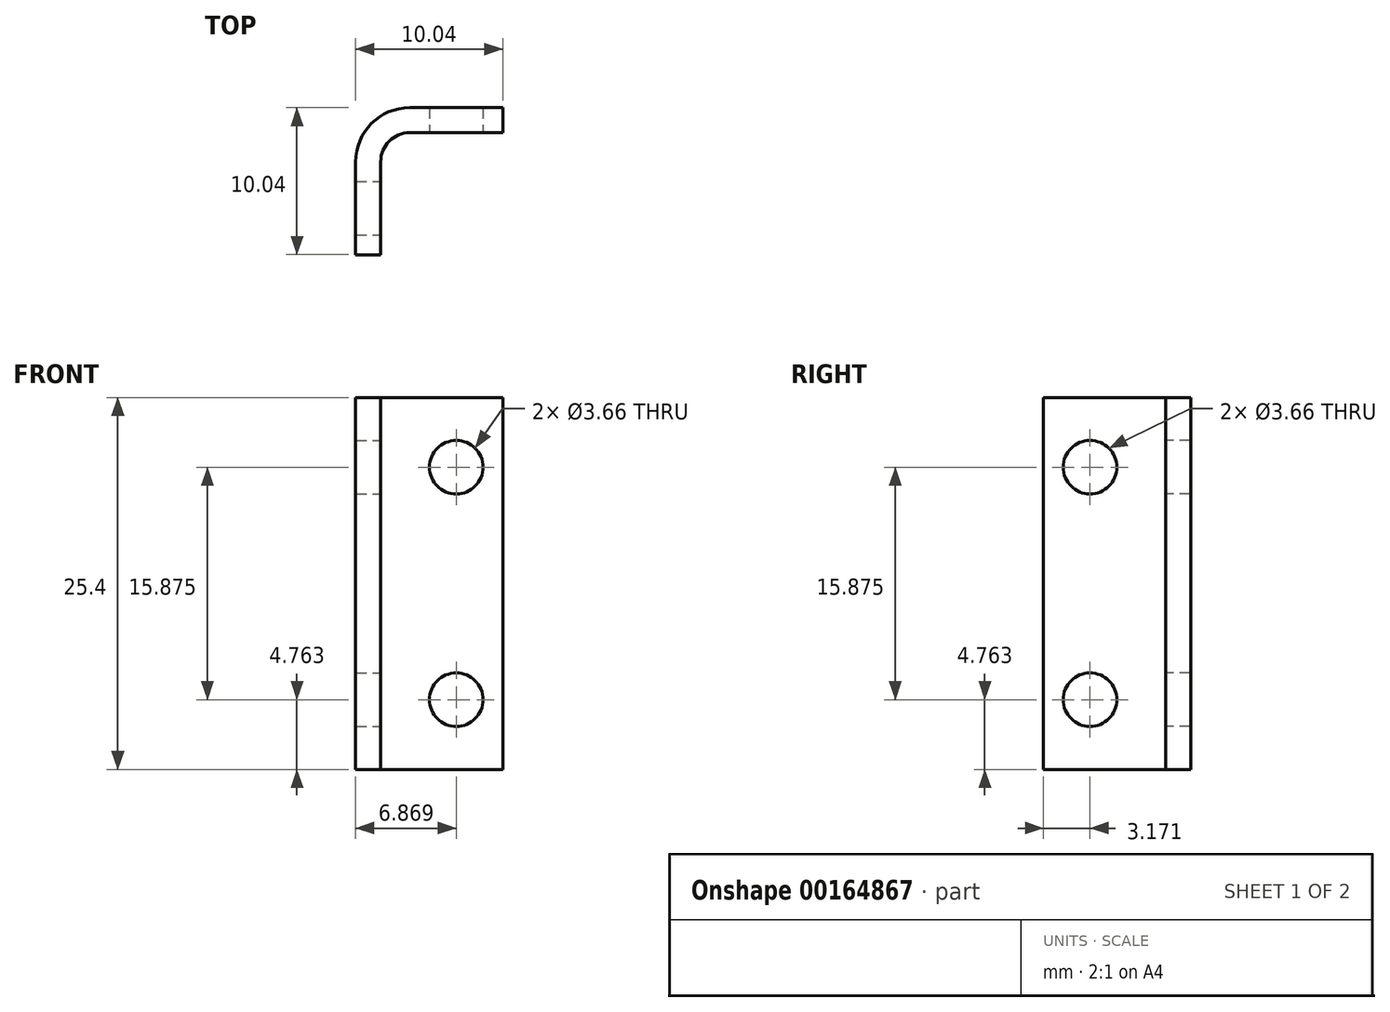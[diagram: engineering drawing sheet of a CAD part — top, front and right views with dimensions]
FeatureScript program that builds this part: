
annotation { "Feature Type Name" : "Feature", "Feature Type Description" : "" }
export const myFeature = defineFeature(function(context is Context, id is Id, definition is map)
    precondition{}
    {
        {
            var Q0;
            Q0=qCreatedBy(makeId("Top.planeOp"),FACE);
            var sketch = newSketch(context, id + "F0", { "sketchPlane" : qUnion([Q0])});
            skLineSegment(sketch, "E0.top", {"start": v(0, -8.33) * mm, "end": v(-1.7, -8.33) * mm});
            skLineSegment(sketch, "E0.left", {"start": v(0, 0) * mm, "end": v(0, -8.33) * mm});
            skLineSegment(sketch, "E0.right", {"start": v(-1.7, 1.7) * mm, "end": v(-1.7, -8.33) * mm});
            skLineSegment(sketch, "E1.bottom", {"start": v(0, 0) * mm, "end": v(8.33, 0) * mm});
            skLineSegment(sketch, "E1.top", {"start": v(-1.7, 1.7) * mm, "end": v(8.33, 1.7) * mm});
            skLineSegment(sketch, "E1.right", {"start": v(8.33, 0) * mm, "end": v(8.33, 1.7) * mm});
            skSolve(sketch);
        }
        {
            var Q0;
            Q0 = qSketchRegion(id + "F0", true);
            extrude(context, id + "F1", {"entities" : qUnion([Q0]), "depth" : 25.4 * mm});
        }
        {
            var Q0;
            Q0=makeQuery(id+"F1.opExtrude","SWEPT_FACE",FACE,{"disambiguationData":[OSD([sQuery(id+"F0.wireOp",EDGE,"E1.bottom")])]});
            var sketch = newSketch(context, id + "F2", { "sketchPlane" : qUnion([Q0])});
            skLineSegment(sketch, "E2.bottom", {"start": v(8.33, 25.4) * mm, "end": v(5.16, 25.4) * mm, "construction": true});
            skLineSegment(sketch, "E2.top", {"start": v(8.33, 20.64) * mm, "end": v(5.16, 20.64) * mm, "construction": true});
            skLineSegment(sketch, "E2.left", {"start": v(8.33, 25.4) * mm, "end": v(8.33, 20.64) * mm, "construction": true});
            skLineSegment(sketch, "E2.right", {"start": v(5.16, 25.4) * mm, "end": v(5.16, 20.64) * mm, "construction": true});
            skLineSegment(sketch, "E3.bottom", {"start": v(8.33, 0) * mm, "end": v(5.16, 0) * mm, "construction": true});
            skLineSegment(sketch, "E3.top", {"start": v(8.33, 4.76) * mm, "end": v(5.16, 4.76) * mm, "construction": true});
            skLineSegment(sketch, "E3.left", {"start": v(8.33, 0) * mm, "end": v(8.33, 4.76) * mm, "construction": true});
            skLineSegment(sketch, "E3.right", {"start": v(5.16, 0) * mm, "end": v(5.16, 4.76) * mm, "construction": true});
            skCircle(sketch, "E4", {"center": v(5.16, 20.64) * mm, "radius": 1.83 * mm});
            skCircle(sketch, "E5", {"center": v(5.16, 4.76) * mm, "radius": 1.83 * mm});
            skSolve(sketch);
        }
        {
            var Q0;
            Q0 = qSketchRegion(id + "F2", true);
            var Q1;
            Q1=makeQuery(id+"F1.opExtrude","SWEPT_FACE",FACE,{"disambiguationData":[OSD([sQuery(id+"F0.wireOp",EDGE,"E1.top")])]});
            extrude(context, id + "F3", {"entities" : qUnion([Q0]), "operationType" : NewBodyOperationType.REMOVE, "endBound" : BoundingType.UP_TO_SURFACE, "oppositeDirection" : true, "endBoundEntityFace" : qUnion([Q1]), "depth" : 25.4 * mm});
        }
        {
            var Q0;
            Q0=makeQuery(id+"F1.opExtrude","SWEPT_FACE",FACE,{"disambiguationData":[OSD([sQuery(id+"F0.wireOp",EDGE,"E0.left")])]});
            var sketch = newSketch(context, id + "F4", { "sketchPlane" : qUnion([Q0])});
            skLineSegment(sketch, "E6.bottom", {"start": v(-8.33, 25.4) * mm, "end": v(-5.16, 25.4) * mm, "construction": true});
            skLineSegment(sketch, "E6.top", {"start": v(-8.33, 20.64) * mm, "end": v(-5.16, 20.64) * mm, "construction": true});
            skLineSegment(sketch, "E6.left", {"start": v(-8.33, 25.4) * mm, "end": v(-8.33, 20.64) * mm, "construction": true});
            skLineSegment(sketch, "E6.right", {"start": v(-5.16, 25.4) * mm, "end": v(-5.16, 20.64) * mm, "construction": true});
            skLineSegment(sketch, "E7.bottom", {"start": v(-8.33, 0) * mm, "end": v(-5.16, 0) * mm, "construction": true});
            skLineSegment(sketch, "E7.top", {"start": v(-8.33, 4.76) * mm, "end": v(-5.16, 4.76) * mm, "construction": true});
            skLineSegment(sketch, "E7.left", {"start": v(-8.33, 0) * mm, "end": v(-8.33, 4.76) * mm, "construction": true});
            skLineSegment(sketch, "E7.right", {"start": v(-5.16, 0) * mm, "end": v(-5.16, 4.76) * mm, "construction": true});
            skCircle(sketch, "E8", {"center": v(-5.16, 20.64) * mm, "radius": 1.83 * mm});
            skCircle(sketch, "E9", {"center": v(-5.16, 4.76) * mm, "radius": 1.83 * mm});
            skSolve(sketch);
        }
        {
            var Q0;
            Q0 = qSketchRegion(id + "F4", true);
            var Q1;
            Q1=makeQuery(id+"F1.opExtrude","SWEPT_FACE",FACE,{"disambiguationData":[OSD([sQuery(id+"F0.wireOp",EDGE,"E0.right")])]});
            extrude(context, id + "F5", {"entities" : qUnion([Q0]), "operationType" : NewBodyOperationType.REMOVE, "endBound" : BoundingType.UP_TO_SURFACE, "oppositeDirection" : true, "endBoundEntityFace" : qUnion([Q1]), "depth" : 25.4 * mm});
        }
        {
            var Q0;
            Q0=makeQuery(id+"F1.opExtrude","SWEPT_EDGE",EDGE,{"disambiguationData":[OSD([sQuery(id+"F0.wireOp",EDGE,"E0.left"),sQuery(id+"F0.wireOp",EDGE,"E1.bottom")])]});
            fillet(context, id + "F6", {"entities" : qUnion([Q0]), "radius" : 1.98 * mm, "tangentPropagation" : true, "allowEdgeOverflow" : false});
        }
        {
            var Q0;
            Q0=makeQuery(id+"F1.opExtrude","SWEPT_EDGE",EDGE,{"disambiguationData":[OSD([sQuery(id+"F0.wireOp",EDGE,"E0.right"),sQuery(id+"F0.wireOp",EDGE,"E1.top")])]});
            fillet(context, id + "F7", {"entities" : qUnion([Q0]), "radius" : 3.7 * mm, "tangentPropagation" : true, "allowEdgeOverflow" : false});
        }
    });
